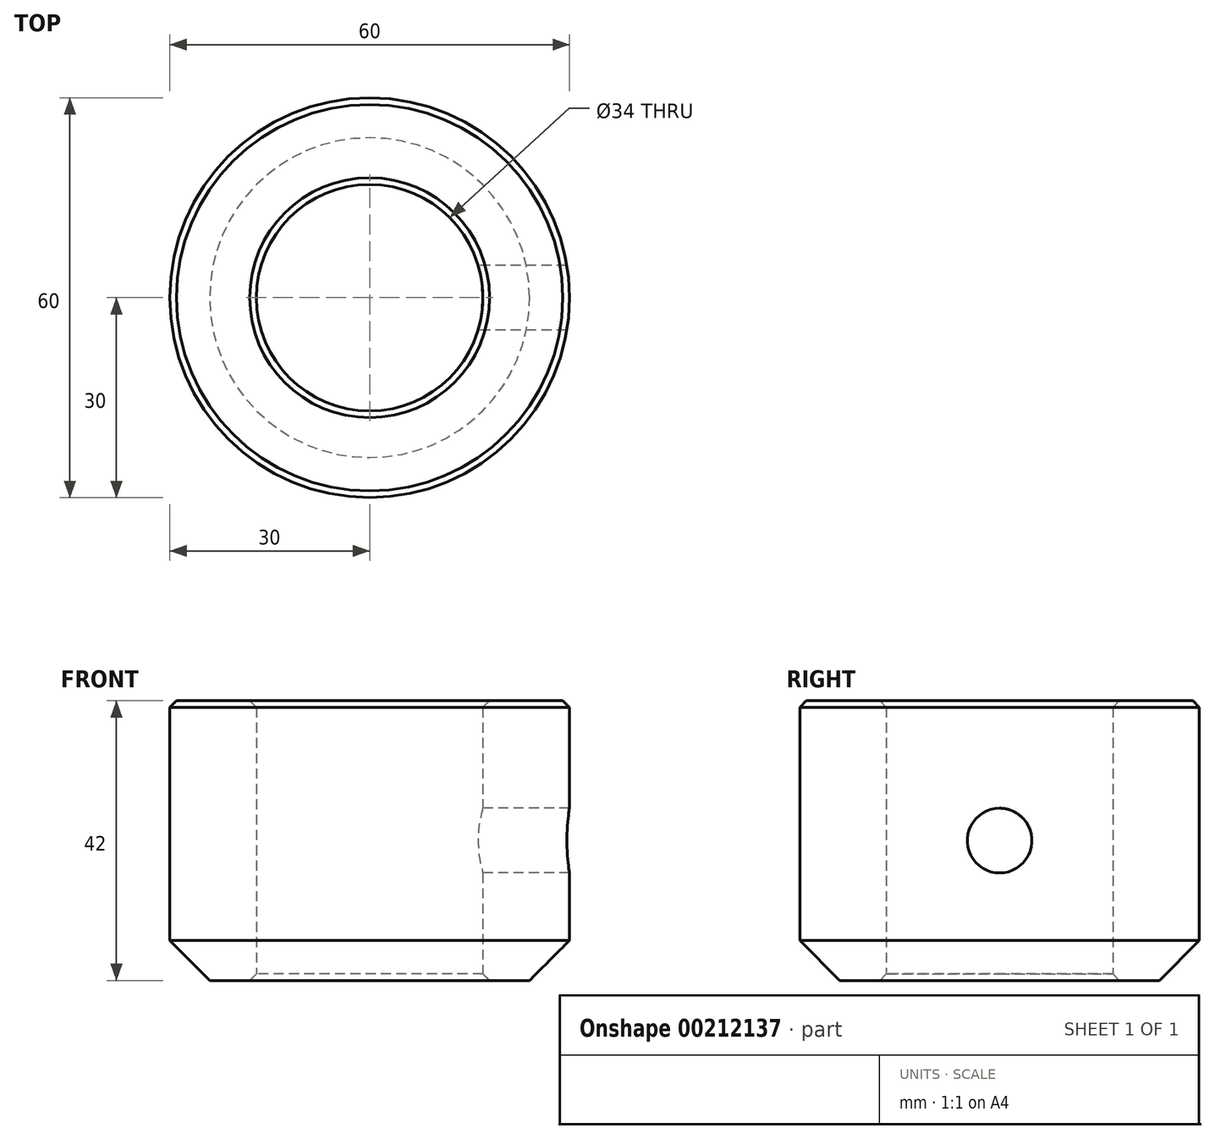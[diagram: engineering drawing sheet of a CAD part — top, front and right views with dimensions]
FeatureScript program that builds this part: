
annotation { "Feature Type Name" : "Feature", "Feature Type Description" : "" }
export const myFeature = defineFeature(function(context is Context, id is Id, definition is map)
    precondition{}
    {
        {
            var Q0;
            Q0=qCreatedBy(makeId("Top.planeOp"),FACE);
            var sketch = newSketch(context, id + "F0", { "sketchPlane" : qUnion([Q0])});
            skCircle(sketch, "E0", {"center": v(0, 0) * mm, "radius": 17 * mm});
            skCircle(sketch, "E1", {"center": v(0, 0) * mm, "radius": 30 * mm});
            skSolve(sketch);
        }
        {
            var Q0;
            Q0=makeQuery(id+"F0.imprint","IMPRINT",FACE,{"disambiguationData":[TD([[makeQuery(id+"F0.imprint","IMPRINT",EDGE,{"derivedFrom":sQuery(id+"F0.wireOp",EDGE,"E0")}),-1.0]])]});
            extrude(context, id + "F1", {"entities" : qUnion([Q0]), "depth" : 42 * mm});
        }
        {
            var Q0;
            Q0=qCreatedBy(makeId("Right.planeOp"),FACE);
            var sketch = newSketch(context, id + "F2", { "sketchPlane" : qUnion([Q0])});
            skCircle(sketch, "E2", {"center": v(0, 21) * mm, "radius": 4.86 * mm});
            skSolve(sketch);
        }
        {
            var Q0;
            Q0=sQuery(id+"F2.wireOp",VERTEX,"E2.center");
            var Q1;
            Q1=makeQuery(id+"F1.opExtrude","SWEPT_BODY",BODY,{"disambiguationData":[OSD([sQuery(id+"F0.wireOp",EDGE,"E0"),sQuery(id+"F0.wireOp",EDGE,"E1")])]});
            hole(context, id + "F3", {"style" : HoleStyle.SIMPLE, "endStyle" : HoleEndStyle.THROUGH, "oppositeDirection" : true, "holeDiameter" : 9.72 * mm, "locations" : qUnion([Q0]), "scope" : qUnion([Q1]), "isTappedThrough" : true});
        }
        {
            var Q0;
            Q0=makeQuery(id+"F1.opExtrude","CAP_EDGE",EDGE,{"disambiguationData":[OSD([sQuery(id+"F0.wireOp",EDGE,"E0")])],"isStart":false});
            var Q1;
            Q1=makeQuery(id+"F1.opExtrude","CAP_EDGE",EDGE,{"disambiguationData":[OSD([sQuery(id+"F0.wireOp",EDGE,"E1")])],"isStart":false});
            var Q2;
            Q2=makeQuery(id+"F3.hole-0.boolean.opBoolean","INTERSECT",EDGE,{"derivedFrom":[makeQuery(id+"F1.opExtrude","SWEPT_FACE",FACE,{"disambiguationData":[OSD([sQuery(id+"F0.wireOp",EDGE,"E1")])]}),makeQuery(id+"F3.hole-0.opRevolve","SWEPT_FACE",FACE,{"disambiguationData":[OSD([sQuery(id+"F3.hole-0.sketch.wireOp",EDGE,"core_line_2")])]})]});
            var Q3;
            Q3=makeQuery(id+"F1.opExtrude","CAP_EDGE",EDGE,{"disambiguationData":[OSD([sQuery(id+"F0.wireOp",EDGE,"E0")])],"isStart":true});
            chamfer(context, id + "F4", {"entities" : qUnion([Q0, Q1, Q2, Q3]), "width" : 1 * mm, "tangentPropagation" : true});
        }
        {
            var Q0;
            Q0=makeQuery(id+"F1.opExtrude","CAP_EDGE",EDGE,{"disambiguationData":[OSD([sQuery(id+"F0.wireOp",EDGE,"E1")])],"isStart":true});
            chamfer(context, id + "F5", {"entities" : qUnion([Q0]), "width" : 6 * mm, "tangentPropagation" : true});
        }
    });
